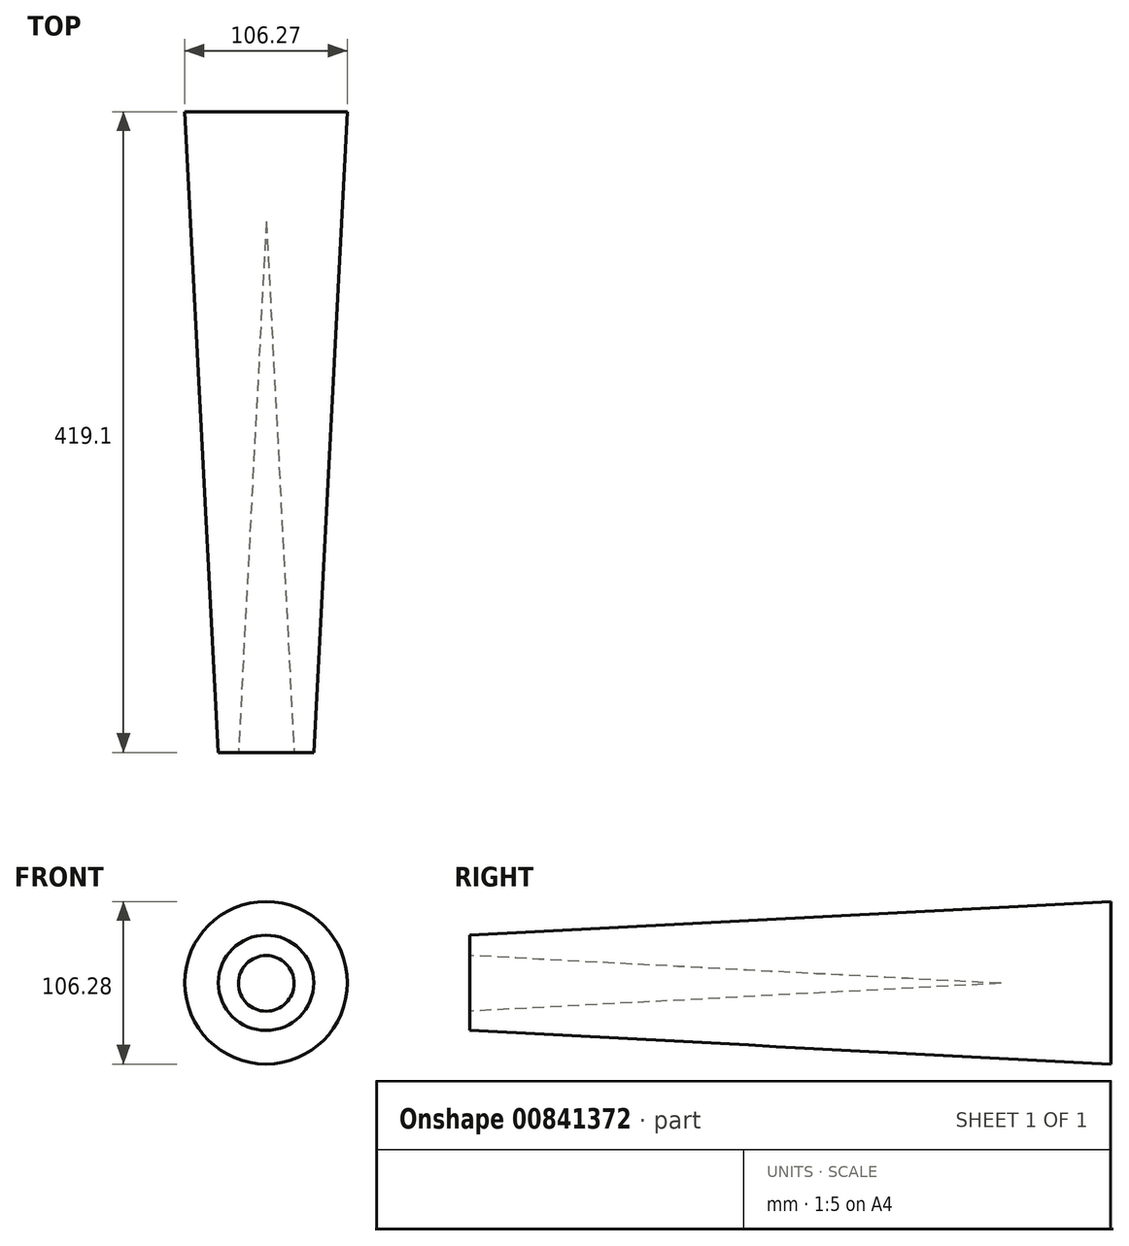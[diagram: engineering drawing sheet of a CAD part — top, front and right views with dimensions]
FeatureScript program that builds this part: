
annotation { "Feature Type Name" : "Feature", "Feature Type Description" : "" }
export const myFeature = defineFeature(function(context is Context, id is Id, definition is map)
    precondition{}
    {
        {
            var Q0;
            Q0=qCreatedBy(makeId("Front.planeOp"),FACE);
            var sketch = newSketch(context, id + "F0", { "sketchPlane" : qUnion([Q0])});
            skCircle(sketch, "E0", {"center": v(-0.15, 0.38) * mm, "radius": 31.17 * mm});
            skCircle(sketch, "E1", {"center": v(0, 0) * mm, "radius": 18.2 * mm});
            skSolve(sketch);
        }
        {
            var Q0;
            Q0 = qSketchRegion(id + "F0", true);
            extrude(context, id + "F1", {"entities" : qUnion([Q0]), "oppositeDirection" : true, "depth" : 419.1 * mm, "offsetDistance" : 25.4 * mm, "hasDraft" : true, "draftAngle" : 3 * degree});
        }
    });
